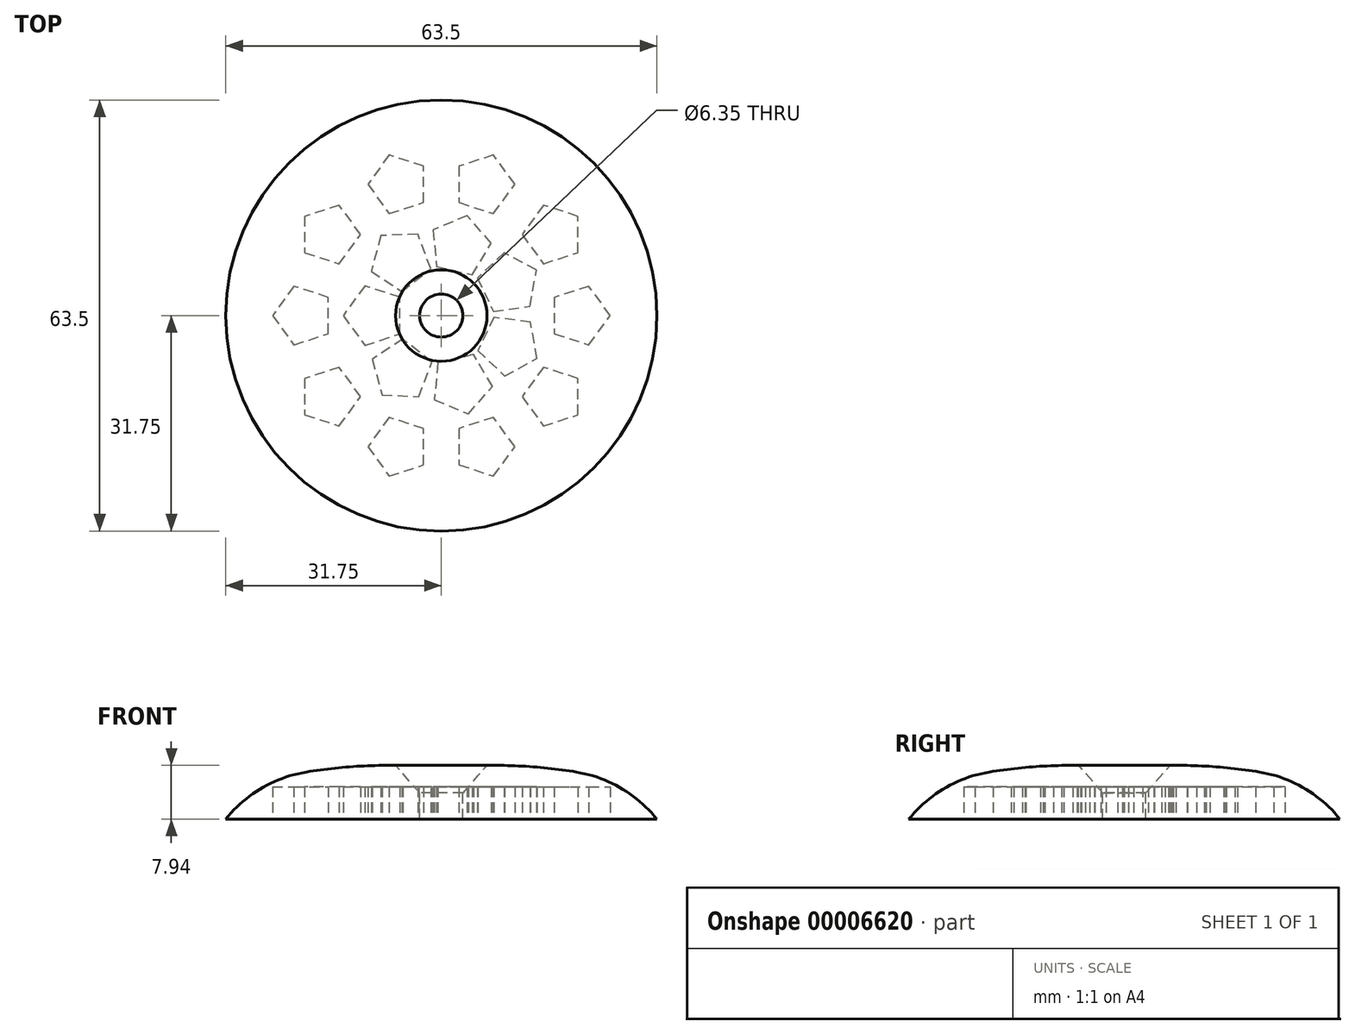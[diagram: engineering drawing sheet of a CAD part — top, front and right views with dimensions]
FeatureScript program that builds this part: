
annotation { "Feature Type Name" : "Feature", "Feature Type Description" : "" }
export const myFeature = defineFeature(function(context is Context, id is Id, definition is map)
    precondition{}
    {
        {
            var Q0;
            Q0=qCreatedBy(makeId("Front.planeOp"),FACE);
            var sketch = newSketch(context, id + "F0", { "sketchPlane" : qUnion([Q0])});
            skLineSegment(sketch, "E0", {"start": v(0, 49.55) * mm, "end": v(0, -55.6) * mm, "construction": true});
            skArc(sketch, "E1", {"start": v(31.75, 4.02) * mm, "mid": v(19.84, 6.95) * mm, "end": v(7.62, 7.94) * mm});
            skLineSegment(sketch, "E2", {"start": v(7.62, 7.94) * mm, "end": v(6.73, 7.94) * mm});
            skLineSegment(sketch, "E3", {"start": v(31.75, 4.02) * mm, "end": v(31.75, 0) * mm});
            skLineSegment(sketch, "E4", {"start": v(31.75, 0) * mm, "end": v(3.18, 0) * mm});
            skLineSegment(sketch, "E5", {"start": v(3.18, 0) * mm, "end": v(3.18, 3.85) * mm});
            skLineSegment(sketch, "E6", {"start": v(3.18, 3.85) * mm, "end": v(6.73, 7.94) * mm});
            skSolve(sketch);
        }
        {
            var Q0;
            Q0 = qSketchRegion(id + "F0", true);
            var Q1;
            Q1=sQuery(id+"F0.wireOp",EDGE,"E0");
            revolve(context, id + "F1", {"entities" : qUnion([Q0]), "axis" : qUnion([Q1]), "revolveType" : RevolveType.FULL});
        }
        {
            var Q0;
            Q0=makeQuery(id+"F1.opRevolve","SWEPT_FACE",FACE,{"disambiguationData":[OSD([sQuery(id+"F0.wireOp",EDGE,"E4")])]});
            var sketch = newSketch(context, id + "F2", { "sketchPlane" : qUnion([Q0])});
            skCircle(sketch, "E7.cCircle", {"center": v(-9.84, 0) * mm, "radius": 3.73 * mm, "construction": true});
            skLineSegment(sketch, "E7.0", {"start": v(-6.1, 2.71) * mm, "end": v(-6.1, -2.71) * mm});
            skLineSegment(sketch, "E7.1", {"start": v(-6.1, -2.71) * mm, "end": v(-11.27, -4.39) * mm});
            skLineSegment(sketch, "E7.2", {"start": v(-11.27, -4.39) * mm, "end": v(-14.46, 0) * mm});
            skLineSegment(sketch, "E7.3", {"start": v(-14.46, 0) * mm, "end": v(-11.27, 4.39) * mm});
            skLineSegment(sketch, "E7.4", {"start": v(-11.27, 4.39) * mm, "end": v(-6.1, 2.71) * mm});
            skPoint(sketch, "E7.0.midPoint", {"position": v(-6.1, 0) * mm});
            skLineSegment(sketch, "E8.1.0", {"start": v(-10.33, -6.53) * mm, "end": v(-5.8, -3.54) * mm});
            skLineSegment(sketch, "E8.1.1", {"start": v(-8.89, -11.76) * mm, "end": v(-10.33, -6.53) * mm});
            skLineSegment(sketch, "E8.1.2", {"start": v(-3.47, -12) * mm, "end": v(-8.89, -11.76) * mm});
            skLineSegment(sketch, "E8.1.3", {"start": v(-1.56, -6.93) * mm, "end": v(-3.47, -12) * mm});
            skLineSegment(sketch, "E8.1.4", {"start": v(-5.8, -3.54) * mm, "end": v(-1.56, -6.93) * mm});
            skCircle(sketch, "E8.1.5", {"center": v(-6, -8.16) * mm, "radius": 3.73 * mm, "construction": true});
            skPoint(sketch, "E8.1.6", {"position": v(-3.68, -5.24) * mm});
            skLineSegment(sketch, "E8.2.0", {"start": v(-1.2, -12.61) * mm, "end": v(-0.72, -7.2) * mm});
            skLineSegment(sketch, "E8.2.1", {"start": v(3.79, -14.74) * mm, "end": v(-1.2, -12.61) * mm});
            skLineSegment(sketch, "E8.2.2", {"start": v(7.36, -10.66) * mm, "end": v(3.79, -14.74) * mm});
            skLineSegment(sketch, "E8.2.3", {"start": v(4.57, -6) * mm, "end": v(7.36, -10.66) * mm});
            skLineSegment(sketch, "E8.2.4", {"start": v(-0.72, -7.2) * mm, "end": v(4.57, -6) * mm});
            skCircle(sketch, "E8.2.5", {"center": v(2.76, -10.24) * mm, "radius": 3.73 * mm, "construction": true});
            skPoint(sketch, "E8.2.6", {"position": v(1.93, -6.6) * mm});
            skLineSegment(sketch, "E8.3.0", {"start": v(9.24, -9.26) * mm, "end": v(5.32, -5.51) * mm});
            skLineSegment(sketch, "E8.3.1", {"start": v(14.02, -6.7) * mm, "end": v(9.24, -9.26) * mm});
            skLineSegment(sketch, "E8.3.2", {"start": v(13.05, -1.35) * mm, "end": v(14.02, -6.7) * mm});
            skLineSegment(sketch, "E8.3.3", {"start": v(7.67, -0.63) * mm, "end": v(13.05, -1.35) * mm});
            skLineSegment(sketch, "E8.3.4", {"start": v(5.32, -5.51) * mm, "end": v(7.67, -0.63) * mm});
            skCircle(sketch, "E8.3.5", {"center": v(9.86, -4.7) * mm, "radius": 3.73 * mm, "construction": true});
            skPoint(sketch, "E8.3.6", {"position": v(6.5, -3.07) * mm});
            skLineSegment(sketch, "E8.4.0", {"start": v(13.13, 0.98) * mm, "end": v(7.75, 0.26) * mm});
            skLineSegment(sketch, "E8.4.1", {"start": v(14.1, 6.32) * mm, "end": v(13.13, 0.98) * mm});
            skLineSegment(sketch, "E8.4.2", {"start": v(9.32, 8.9) * mm, "end": v(14.1, 6.32) * mm});
            skLineSegment(sketch, "E8.4.3", {"start": v(5.4, 5.15) * mm, "end": v(9.32, 8.9) * mm});
            skLineSegment(sketch, "E8.4.4", {"start": v(7.75, 0.26) * mm, "end": v(5.4, 5.15) * mm});
            skCircle(sketch, "E8.4.5", {"center": v(9.94, 4.32) * mm, "radius": 3.73 * mm, "construction": true});
            skPoint(sketch, "E8.4.6", {"position": v(6.58, 2.7) * mm});
            skLineSegment(sketch, "E8.5.0", {"start": v(7.55, 10.42) * mm, "end": v(4.76, 5.76) * mm});
            skLineSegment(sketch, "E8.5.1", {"start": v(3.98, 14.5) * mm, "end": v(7.55, 10.42) * mm});
            skLineSegment(sketch, "E8.5.2", {"start": v(-1.01, 12.37) * mm, "end": v(3.98, 14.5) * mm});
            skLineSegment(sketch, "E8.5.3", {"start": v(-0.53, 6.97) * mm, "end": v(-1.01, 12.37) * mm});
            skLineSegment(sketch, "E8.5.4", {"start": v(4.76, 5.76) * mm, "end": v(-0.53, 6.97) * mm});
            skCircle(sketch, "E8.5.5", {"center": v(2.95, 10) * mm, "radius": 3.73 * mm, "construction": true});
            skPoint(sketch, "E8.5.6", {"position": v(2.12, 6.37) * mm});
            skLineSegment(sketch, "E8.6.0", {"start": v(-3.31, 11.93) * mm, "end": v(-1.4, 6.85) * mm});
            skLineSegment(sketch, "E8.6.1", {"start": v(-8.73, 11.7) * mm, "end": v(-3.31, 11.93) * mm});
            skLineSegment(sketch, "E8.6.2", {"start": v(-10.18, 6.46) * mm, "end": v(-8.73, 11.7) * mm});
            skLineSegment(sketch, "E8.6.3", {"start": v(-5.65, 3.47) * mm, "end": v(-10.18, 6.46) * mm});
            skLineSegment(sketch, "E8.6.4", {"start": v(-1.4, 6.85) * mm, "end": v(-5.65, 3.47) * mm});
            skCircle(sketch, "E8.6.5", {"center": v(-5.86, 8.08) * mm, "radius": 3.73 * mm, "construction": true});
            skPoint(sketch, "E8.6.6", {"position": v(-3.53, 5.16) * mm});
            skPoint(sketch, "E8.center", {"position": v(0.54, -0.1) * mm});
            skLineSegment(sketch, "E9", {"start": v(0, 0) * mm, "end": v(-34.65, 0) * mm, "construction": true});
            skCircle(sketch, "E10.cCircle", {"center": v(-20.32, 0) * mm, "radius": 3.68 * mm, "construction": true});
            skLineSegment(sketch, "E10.0", {"start": v(-16.64, 2.67) * mm, "end": v(-16.64, -2.67) * mm});
            skLineSegment(sketch, "E10.1", {"start": v(-16.64, -2.67) * mm, "end": v(-21.72, -4.32) * mm});
            skLineSegment(sketch, "E10.2", {"start": v(-21.72, -4.32) * mm, "end": v(-24.87, 0) * mm});
            skLineSegment(sketch, "E10.3", {"start": v(-24.87, 0) * mm, "end": v(-21.72, 4.32) * mm});
            skLineSegment(sketch, "E10.4", {"start": v(-21.72, 4.32) * mm, "end": v(-16.64, 2.67) * mm});
            skPoint(sketch, "E10.0.midPoint", {"position": v(-16.64, 0) * mm});
            skLineSegment(sketch, "E11.1.0", {"start": v(-15.03, -16.27) * mm, "end": v(-20.12, -14.62) * mm});
            skCircle(sketch, "E11.1.1", {"center": v(-16.44, -11.94) * mm, "radius": 3.68 * mm, "construction": true});
            skLineSegment(sketch, "E11.1.2", {"start": v(-11.9, -11.94) * mm, "end": v(-15.03, -16.27) * mm});
            skLineSegment(sketch, "E11.1.3", {"start": v(-20.12, -14.62) * mm, "end": v(-20.12, -9.27) * mm});
            skLineSegment(sketch, "E11.1.4", {"start": v(-15.03, -7.62) * mm, "end": v(-11.9, -11.94) * mm});
            skLineSegment(sketch, "E11.1.5", {"start": v(-20.12, -9.27) * mm, "end": v(-15.03, -7.62) * mm});
            skPoint(sketch, "E11.1.6", {"position": v(-13.46, -9.78) * mm});
            skPoint(sketch, "E11.1.7", {"position": v(0.5, 0.24) * mm});
            skLineSegment(sketch, "E11.2.0", {"start": v(-2.6, -22) * mm, "end": v(-7.68, -23.65) * mm});
            skCircle(sketch, "E11.2.1", {"center": v(-6.28, -19.33) * mm, "radius": 3.68 * mm, "construction": true});
            skLineSegment(sketch, "E11.2.2", {"start": v(-2.6, -16.65) * mm, "end": v(-2.6, -22) * mm});
            skLineSegment(sketch, "E11.2.3", {"start": v(-7.68, -23.65) * mm, "end": v(-10.83, -19.33) * mm});
            skLineSegment(sketch, "E11.2.4", {"start": v(-7.68, -15) * mm, "end": v(-2.6, -16.65) * mm});
            skLineSegment(sketch, "E11.2.5", {"start": v(-10.83, -19.33) * mm, "end": v(-7.68, -15) * mm});
            skPoint(sketch, "E11.2.6", {"position": v(-5.14, -15.83) * mm});
            skPoint(sketch, "E11.2.7", {"position": v(0.26, 0.49) * mm});
            skLineSegment(sketch, "E11.3.0", {"start": v(10.83, -19.33) * mm, "end": v(7.68, -23.65) * mm});
            skCircle(sketch, "E11.3.1", {"center": v(6.28, -19.33) * mm, "radius": 3.68 * mm, "construction": true});
            skLineSegment(sketch, "E11.3.2", {"start": v(7.68, -15) * mm, "end": v(10.83, -19.33) * mm});
            skLineSegment(sketch, "E11.3.3", {"start": v(7.68, -23.65) * mm, "end": v(2.6, -22) * mm});
            skLineSegment(sketch, "E11.3.4", {"start": v(2.6, -16.65) * mm, "end": v(7.68, -15) * mm});
            skLineSegment(sketch, "E11.3.5", {"start": v(2.6, -22) * mm, "end": v(2.6, -16.65) * mm});
            skPoint(sketch, "E11.3.6", {"position": v(5.14, -15.83) * mm});
            skPoint(sketch, "E11.3.7", {"position": v(-0.08, 0.55) * mm});
            skLineSegment(sketch, "E11.4.0", {"start": v(20.12, -9.27) * mm, "end": v(20.12, -14.62) * mm});
            skCircle(sketch, "E11.4.1", {"center": v(16.44, -11.94) * mm, "radius": 3.68 * mm, "construction": true});
            skLineSegment(sketch, "E11.4.2", {"start": v(15.03, -7.62) * mm, "end": v(20.12, -9.27) * mm});
            skLineSegment(sketch, "E11.4.3", {"start": v(20.12, -14.62) * mm, "end": v(15.03, -16.27) * mm});
            skLineSegment(sketch, "E11.4.4", {"start": v(11.9, -11.94) * mm, "end": v(15.03, -7.62) * mm});
            skLineSegment(sketch, "E11.4.5", {"start": v(15.03, -16.27) * mm, "end": v(11.9, -11.94) * mm});
            skPoint(sketch, "E11.4.6", {"position": v(13.46, -9.78) * mm});
            skPoint(sketch, "E11.4.7", {"position": v(-0.38, 0.4) * mm});
            skLineSegment(sketch, "E11.5.0", {"start": v(21.72, 4.32) * mm, "end": v(24.87, 0) * mm});
            skCircle(sketch, "E11.5.1", {"center": v(20.32, 0) * mm, "radius": 3.68 * mm, "construction": true});
            skLineSegment(sketch, "E11.5.2", {"start": v(16.64, 2.67) * mm, "end": v(21.72, 4.32) * mm});
            skLineSegment(sketch, "E11.5.3", {"start": v(24.87, 0) * mm, "end": v(21.72, -4.32) * mm});
            skLineSegment(sketch, "E11.5.4", {"start": v(16.64, -2.67) * mm, "end": v(16.64, 2.67) * mm});
            skLineSegment(sketch, "E11.5.5", {"start": v(21.72, -4.32) * mm, "end": v(16.64, -2.67) * mm});
            skPoint(sketch, "E11.5.6", {"position": v(16.64, 0) * mm});
            skPoint(sketch, "E11.5.7", {"position": v(-0.54, 0.1) * mm});
            skLineSegment(sketch, "E11.6.0", {"start": v(15.03, 16.27) * mm, "end": v(20.12, 14.62) * mm});
            skCircle(sketch, "E11.6.1", {"center": v(16.44, 11.94) * mm, "radius": 3.68 * mm, "construction": true});
            skLineSegment(sketch, "E11.6.2", {"start": v(11.9, 11.94) * mm, "end": v(15.03, 16.27) * mm});
            skLineSegment(sketch, "E11.6.3", {"start": v(20.12, 14.62) * mm, "end": v(20.12, 9.27) * mm});
            skLineSegment(sketch, "E11.6.4", {"start": v(15.03, 7.62) * mm, "end": v(11.9, 11.94) * mm});
            skLineSegment(sketch, "E11.6.5", {"start": v(20.12, 9.27) * mm, "end": v(15.03, 7.62) * mm});
            skPoint(sketch, "E11.6.6", {"position": v(13.46, 9.78) * mm});
            skPoint(sketch, "E11.6.7", {"position": v(-0.5, -0.24) * mm});
            skLineSegment(sketch, "E11.7.0", {"start": v(2.6, 22) * mm, "end": v(7.68, 23.65) * mm});
            skCircle(sketch, "E11.7.1", {"center": v(6.28, 19.33) * mm, "radius": 3.68 * mm, "construction": true});
            skLineSegment(sketch, "E11.7.2", {"start": v(2.6, 16.65) * mm, "end": v(2.6, 22) * mm});
            skLineSegment(sketch, "E11.7.3", {"start": v(7.68, 23.65) * mm, "end": v(10.83, 19.33) * mm});
            skLineSegment(sketch, "E11.7.4", {"start": v(7.68, 15) * mm, "end": v(2.6, 16.65) * mm});
            skLineSegment(sketch, "E11.7.5", {"start": v(10.83, 19.33) * mm, "end": v(7.68, 15) * mm});
            skPoint(sketch, "E11.7.6", {"position": v(5.14, 15.83) * mm});
            skPoint(sketch, "E11.7.7", {"position": v(-0.26, -0.49) * mm});
            skLineSegment(sketch, "E11.8.0", {"start": v(-10.83, 19.33) * mm, "end": v(-7.68, 23.65) * mm});
            skCircle(sketch, "E11.8.1", {"center": v(-6.28, 19.33) * mm, "radius": 3.68 * mm, "construction": true});
            skLineSegment(sketch, "E11.8.2", {"start": v(-7.68, 15) * mm, "end": v(-10.83, 19.33) * mm});
            skLineSegment(sketch, "E11.8.3", {"start": v(-7.68, 23.65) * mm, "end": v(-2.6, 22) * mm});
            skLineSegment(sketch, "E11.8.4", {"start": v(-2.6, 16.65) * mm, "end": v(-7.68, 15) * mm});
            skLineSegment(sketch, "E11.8.5", {"start": v(-2.6, 22) * mm, "end": v(-2.6, 16.65) * mm});
            skPoint(sketch, "E11.8.6", {"position": v(-5.14, 15.83) * mm});
            skPoint(sketch, "E11.8.7", {"position": v(0.08, -0.55) * mm});
            skLineSegment(sketch, "E11.9.0", {"start": v(-20.12, 9.27) * mm, "end": v(-20.12, 14.62) * mm});
            skCircle(sketch, "E11.9.1", {"center": v(-16.44, 11.94) * mm, "radius": 3.68 * mm, "construction": true});
            skLineSegment(sketch, "E11.9.2", {"start": v(-15.03, 7.62) * mm, "end": v(-20.12, 9.27) * mm});
            skLineSegment(sketch, "E11.9.3", {"start": v(-20.12, 14.62) * mm, "end": v(-15.03, 16.27) * mm});
            skLineSegment(sketch, "E11.9.4", {"start": v(-11.9, 11.94) * mm, "end": v(-15.03, 7.62) * mm});
            skLineSegment(sketch, "E11.9.5", {"start": v(-15.03, 16.27) * mm, "end": v(-11.9, 11.94) * mm});
            skPoint(sketch, "E11.9.6", {"position": v(-13.46, 9.78) * mm});
            skPoint(sketch, "E11.9.7", {"position": v(0.38, -0.4) * mm});
            skPoint(sketch, "E11.center", {"position": v(0, 0) * mm});
            skSolve(sketch);
        }
        {
            var Q0;
            Q0 = qSketchRegion(id + "F2", true);
            var Q1;
            Q1=makeQuery(id+"F1.opRevolve","SWEPT_FACE",FACE,{"disambiguationData":[OSD([sQuery(id+"F0.wireOp",EDGE,"E1")])]});
            extrude(context, id + "F3", {"entities" : qUnion([Q0]), "operationType" : NewBodyOperationType.REMOVE, "oppositeDirection" : true, "endBoundEntity" : qUnion([Q1]), "depth" : 4.76 * mm});
        }
        {
            var Q0;
            Q0=makeQuery(id+"F1.opRevolve","SWEPT_EDGE",EDGE,{"disambiguationData":[OSD([sQuery(id+"F0.wireOp",EDGE,"E1"),sQuery(id+"F0.wireOp",EDGE,"E3")])]});
            fillet(context, id + "F4", {"entities" : qUnion([Q0]), "radius" : 19.05 * mm, "tangentPropagation" : true, "allowEdgeOverflow" : false});
        }
    });
